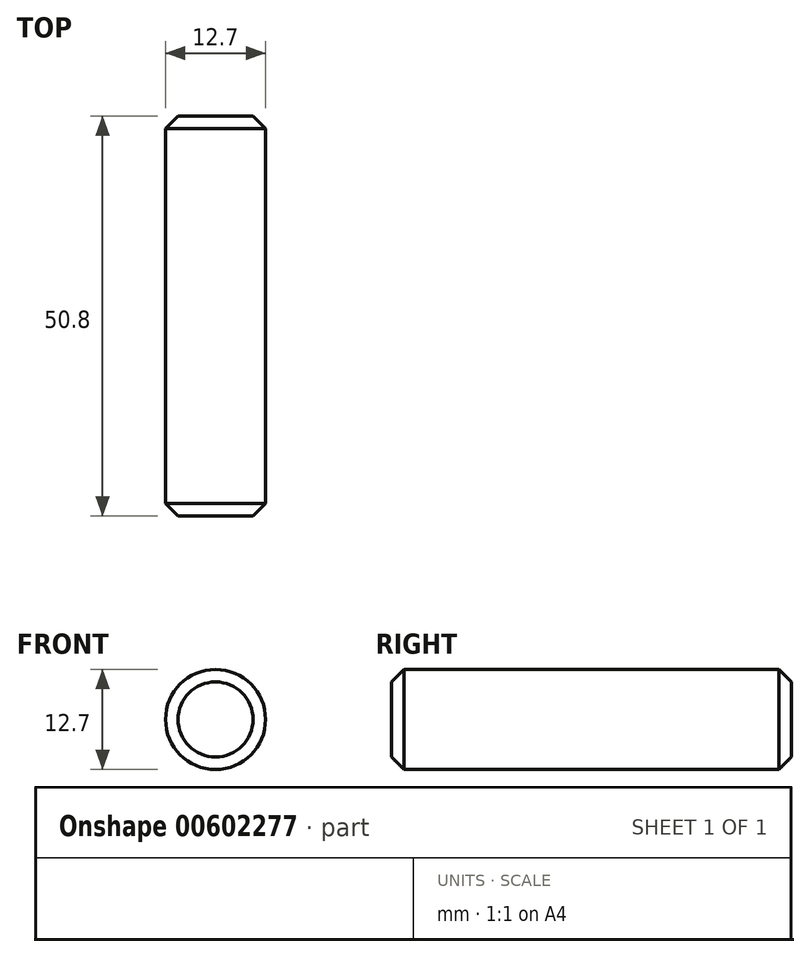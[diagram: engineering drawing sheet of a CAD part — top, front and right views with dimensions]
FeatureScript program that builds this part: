
annotation { "Feature Type Name" : "Feature", "Feature Type Description" : "" }
export const myFeature = defineFeature(function(context is Context, id is Id, definition is map)
    precondition{}
    {
        {
            var Q0;
            Q0=qCreatedBy(makeId("Front.planeOp"),FACE);
            var sketch = newSketch(context, id + "F0", { "sketchPlane" : qUnion([Q0])});
            skCircle(sketch, "E0", {"center": v(0, 0) * mm, "radius": 4.76 * mm});
            skCircle(sketch, "E1", {"center": v(0, 0) * mm, "radius": 6.35 * mm});
            skSolve(sketch);
        }
        {
            var Q0;
            Q0 = qSketchRegion(id + "F0", true);
            var Q1;
            Q1=makeQuery(id+"F0.imprint","IMPRINT",FACE,{"disambiguationData":[TD([[makeQuery(id+"F0.imprint","IMPRINT",EDGE,{"derivedFrom":sQuery(id+"F0.wireOp",EDGE,"E0")}),1.0]])]});
            extrude(context, id + "F1", {"entities" : qUnion([Q0, Q1]), "depth" : 50.8 * mm, "offsetDistance" : 25.4 * mm});
        }
        {
            var Q0;
            Q0=makeQuery(id+"F1.opExtrude","CAP_EDGE",EDGE,{"disambiguationData":[OSD([sQuery(id+"F0.wireOp",EDGE,"E1")])],"isStart":false});
            var Q1;
            Q1=makeQuery(id+"F1.opExtrude","CAP_EDGE",EDGE,{"disambiguationData":[OSD([sQuery(id+"F0.wireOp",EDGE,"E1")])],"isStart":true});
            chamfer(context, id + "F2", {"entities" : qUnion([Q0, Q1]), "chamferType" : ChamferType.OFFSET_ANGLE, "width" : 1.59 * mm, "oppositeDirection" : false, "angle" : 45 * degree, "tangentPropagation" : true});
        }
    });
